# Revit family: i-Vent 2000E
name_source: partatom
category: Оборудование
revit_build: Autodesk Revit 2017 (Build: 20170118_1100(x64)
units: mm (PartAtom-declared; Revit-internal decimal feet)

## family parameters
Всегда вертикально = Да
На основе рабочей плоскости = Нет
Общий = Нет
При загрузке вырезать с полостями = Нет
Размер круглого соединителя = Использовать диаметр
Тип детали = Нормальный
Точка расчета площади = Нет

## types (1)
- i-Vent 2000E
    R = 158 мм
    URL = https://turkov.ru
    Вход = 315 мм
    Изготовитель = Turkov
    Нагреватель 12 кВт = Нагреватель : 12 кВт (380В)
    Нагреватель 15 кВт = Нагреватель : 15 кВт (380В)
    Нагреватель 18 кВт = Нагреватель : 18 кВт (380В)
    Нагреватель 21 кВт = Нагреватель : 21 кВт (380В)
    Нагреватель 24 кВт = Нагреватель : 24 кВт (380В)
    Нагреватель 27 кВт = Нагреватель : 27 кВт (380В)
    Нагреватель 3 кВт = Нагреватель : 4.5 кВт (220В)
    Нагреватель 30 кВт = Нагреватель : 30 кВт (380В)
    Нагреватель 36 кВт = Нагреватель : 36 кВт (380В)
    Нагреватель 4500 Вт = Нагреватель : 4.5 кВт (220В)
    Нагреватель 6 кВт = Нагреватель : 6.0 кВт (380В)
    Нагреватель 7500 Вт = Нагреватель : 7.5 кВт (380В)
    Нагреватель 9 кВт = Нагреватель : 9 кВт (380В)
